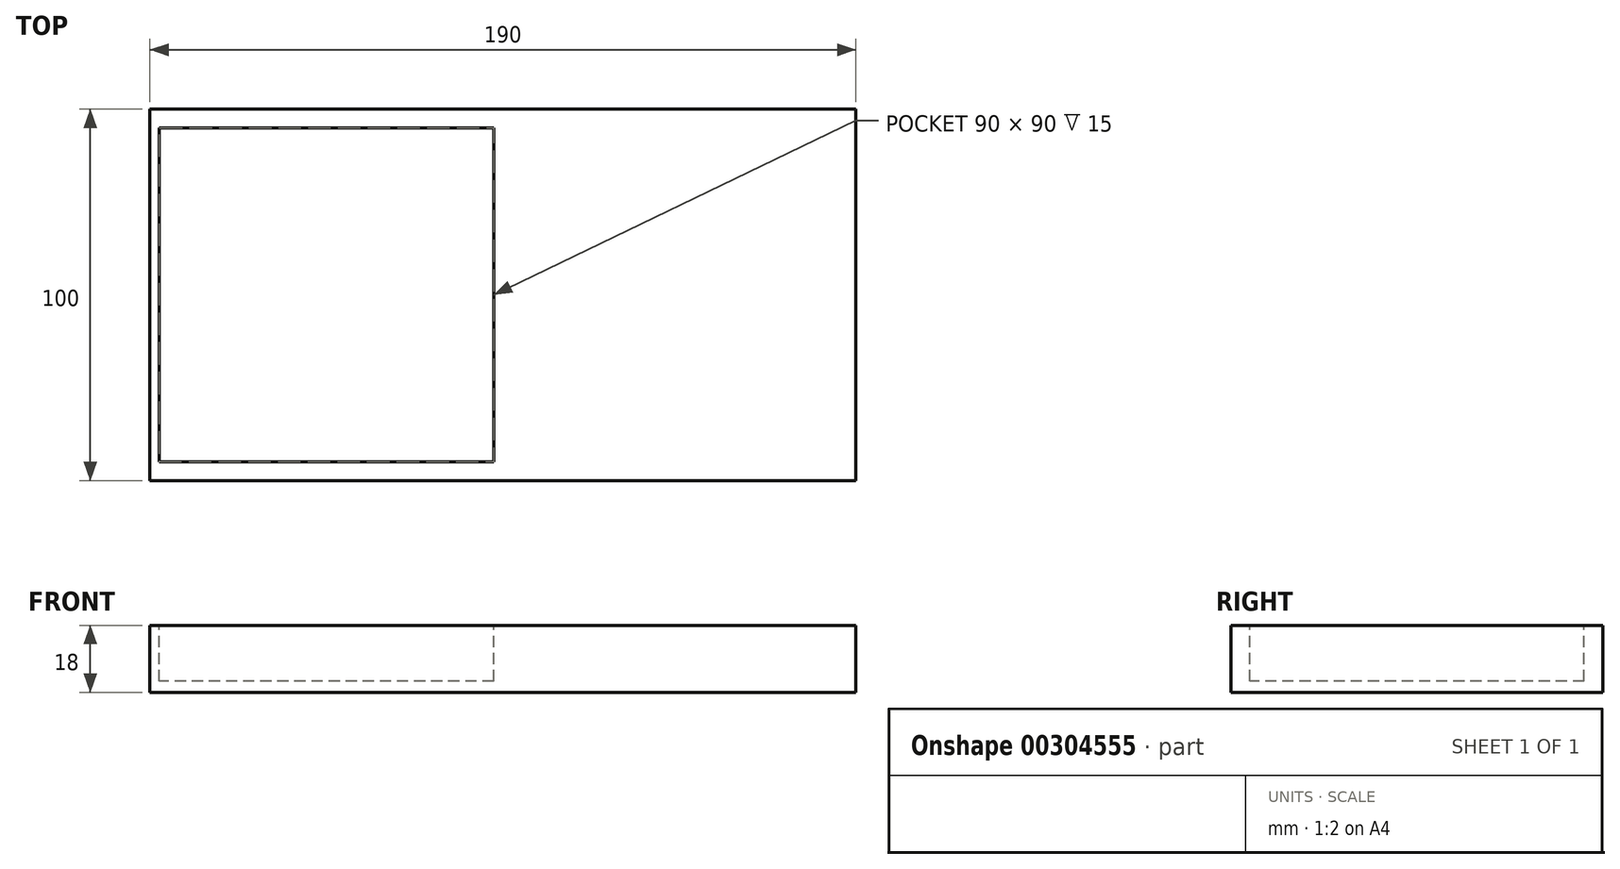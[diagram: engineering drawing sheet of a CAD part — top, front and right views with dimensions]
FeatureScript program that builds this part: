
annotation { "Feature Type Name" : "Feature", "Feature Type Description" : "" }
export const myFeature = defineFeature(function(context is Context, id is Id, definition is map)
    precondition{}
    {
        {
            var Q0;
            Q0=qCreatedBy(makeId("Top.planeOp"),FACE);
            var sketch = newSketch(context, id + "F0", { "sketchPlane" : qUnion([Q0])});
            skPoint(sketch, "E0.middle", {"position": v(0, 0) * mm});
            skLineSegment(sketch, "E1.bottom", {"start": v(95, -50) * mm, "end": v(-95, -50) * mm});
            skLineSegment(sketch, "E1.top", {"start": v(95, 50) * mm, "end": v(-95, 50) * mm});
            skLineSegment(sketch, "E1.left", {"start": v(95, -50) * mm, "end": v(95, 50) * mm});
            skLineSegment(sketch, "E1.right", {"start": v(-95, -50) * mm, "end": v(-95, 50) * mm});
            skSolve(sketch);
        }
        {
            var Q0;
            Q0=makeQuery(id+"F0.imprint","IMPRINT",FACE,{"disambiguationData":[TD([[makeQuery(id+"F0.imprint","IMPRINT",EDGE,{"derivedFrom":sQuery(id+"F0.wireOp",EDGE,"E1.bottom")}),-1.0]])]});
            extrude(context, id + "F1", {"entities" : qUnion([Q0]), "depth" : 18 * mm});
        }
        {
            var Q0;
            Q0=makeQuery(id+"F1.opExtrude","CAP_FACE",FACE,{"disambiguationData":[OSD([sQuery(id+"F0.wireOp",EDGE,"E1.bottom"),sQuery(id+"F0.wireOp",EDGE,"E1.top"),sQuery(id+"F0.wireOp",EDGE,"E1.left"),sQuery(id+"F0.wireOp",EDGE,"E1.right")])],"isStart":false});
            var sketch = newSketch(context, id + "F2", { "sketchPlane" : qUnion([Q0])});
            skLineSegment(sketch, "E2", {"start": v(0, 50) * mm, "end": v(0, -50) * mm});
            skLineSegment(sketch, "E3", {"start": v(0, 50) * mm, "end": v(-95, -50) * mm, "construction": true});
            skLineSegment(sketch, "E4.bottom", {"start": v(-2.5, 45) * mm, "end": v(-92.5, 45) * mm});
            skLineSegment(sketch, "E4.top", {"start": v(-2.5, -45) * mm, "end": v(-92.5, -45) * mm});
            skLineSegment(sketch, "E4.left", {"start": v(-2.5, 45) * mm, "end": v(-2.5, -45) * mm});
            skLineSegment(sketch, "E4.right", {"start": v(-92.5, 45) * mm, "end": v(-92.5, -45) * mm});
            skPoint(sketch, "E4.middle", {"position": v(-47.5, 0) * mm});
            skSolve(sketch);
        }
        {
            var Q0;
            Q0 = qSketchRegion(id + "F2", true);
            extrude(context, id + "F3", {"entities" : qUnion([Q0]), "operationType" : NewBodyOperationType.REMOVE, "oppositeDirection" : true, "depth" : 15 * mm});
        }
    });
